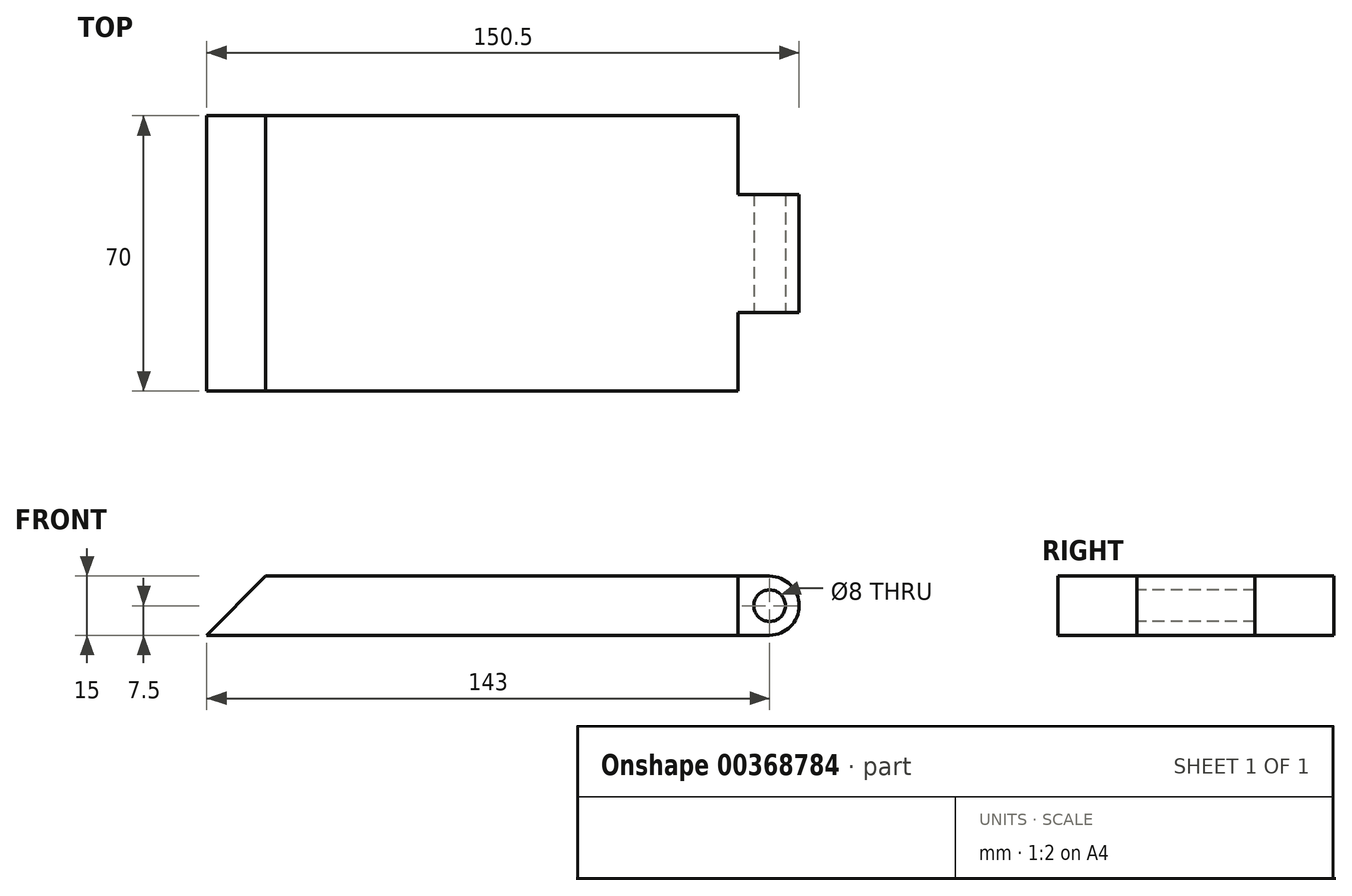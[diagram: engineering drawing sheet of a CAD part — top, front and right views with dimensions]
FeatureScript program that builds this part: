
annotation { "Feature Type Name" : "Feature", "Feature Type Description" : "" }
export const myFeature = defineFeature(function(context is Context, id is Id, definition is map)
    precondition{}
    {
        {
            var Q0;
            Q0=qCreatedBy(makeId("Front.planeOp"),FACE);
            var sketch = newSketch(context, id + "F0", { "sketchPlane" : qUnion([Q0])});
            skLineSegment(sketch, "E0.bottom", {"start": v(-4, 7.5) * mm, "end": v(4, 7.5) * mm});
            skLineSegment(sketch, "E0.top", {"start": v(-4, -7.5) * mm, "end": v(4, -7.5) * mm});
            skLineSegment(sketch, "E0.left", {"start": v(-4, 7.5) * mm, "end": v(-4, -7.5) * mm});
            skLineSegment(sketch, "E0.right", {"start": v(4, 7.5) * mm, "end": v(4, -7.5) * mm});
            skPoint(sketch, "E0.middle", {"position": v(0, 0) * mm});
            skCircle(sketch, "E1", {"center": v(4, 0) * mm, "radius": 7.5 * mm});
            skCircle(sketch, "E2", {"center": v(4, 0) * mm, "radius": 4 * mm});
            skSolve(sketch);
        }
        {
            var Q0;
            Q0 = qSketchRegion(id + "F0", true);
            extrude(context, id + "F1", {"entities" : qUnion([Q0]), "oppositeDirection" : true, "depth" : 15 * mm});
        }
        {
            var Q0;
            Q0=makeQuery(id+"F1.opExtrude","CAP_FACE",FACE,{"disambiguationData":[OSD([sQuery(id+"F0.wireOp",EDGE,"E0.bottom"),sQuery(id+"F0.wireOp",EDGE,"E0.top"),sQuery(id+"F0.wireOp",EDGE,"E0.left"),sQuery(id+"F0.wireOp",EDGE,"E1"),sQuery(id+"F0.wireOp",EDGE,"E2")])],"isStart":true});
            extrude(context, id + "F2", {"entities" : qUnion([Q0]), "operationType" : NewBodyOperationType.ADD, "depth" : 15 * mm});
        }
        {
            var Q0;
            {var subQ0=sQuery(id+"F0.wireOp",EDGE,"E0.left");Q0=makeQuery(id+"F2.boolean.opBoolean","MERGE",FACE,{"derivedFrom":[makeQuery(id+"F1.opExtrude","SWEPT_FACE",FACE,{"disambiguationData":[OSD([subQ0])]}),makeQuery(id+"F2.opExtrude","SWEPT_FACE",FACE,{"disambiguationData":[OSD([subQ0])]})]});}
            var sketch = newSketch(context, id + "F3", { "sketchPlane" : qUnion([Q0])});
            skLineSegment(sketch, "E3.bottom", {"start": v(-35, 7.5) * mm, "end": v(35, 7.5) * mm});
            skLineSegment(sketch, "E3.top", {"start": v(-35, -7.5) * mm, "end": v(35, -7.5) * mm});
            skLineSegment(sketch, "E3.left", {"start": v(-35, 7.5) * mm, "end": v(-35, -7.5) * mm});
            skLineSegment(sketch, "E3.right", {"start": v(35, 7.5) * mm, "end": v(35, -7.5) * mm});
            skPoint(sketch, "E3.middle", {"position": v(0, 0) * mm});
            skSolve(sketch);
        }
        {
            var Q0;
            Q0 = qSketchRegion(id + "F3", true);
            extrude(context, id + "F4", {"entities" : qUnion([Q0]), "operationType" : NewBodyOperationType.ADD, "depth" : 120 * mm});
        }
        {
            var Q0;
            Q0=makeQuery(id+"F4.opExtrude","SWEPT_FACE",FACE,{"disambiguationData":[OSD([sQuery(id+"F3.wireOp",EDGE,"E3.right")])]});
            var sketch = newSketch(context, id + "F5", { "sketchPlane" : qUnion([Q0])});
            skLineSegment(sketch, "E4", {"start": v(-124, -7.5) * mm, "end": v(-139, -7.5) * mm});
            skLineSegment(sketch, "E5", {"start": v(-139, -7.5) * mm, "end": v(-124, 7.5) * mm});
            skSolve(sketch);
        }
        {
            var Q0;
            Q0=makeQuery(id+"F5.imprint","IMPRINT",FACE,{"disambiguationData":[TD([[makeQuery(id+"F5.imprint","IMPRINT",EDGE,{"derivedFrom":sQuery(id+"F5.wireOp",EDGE,"E4")}),-1.0]])]});
            extrude(context, id + "F6", {"entities" : qUnion([Q0]), "operationType" : NewBodyOperationType.ADD, "oppositeDirection" : true, "depth" : 70 * mm});
        }
    });
